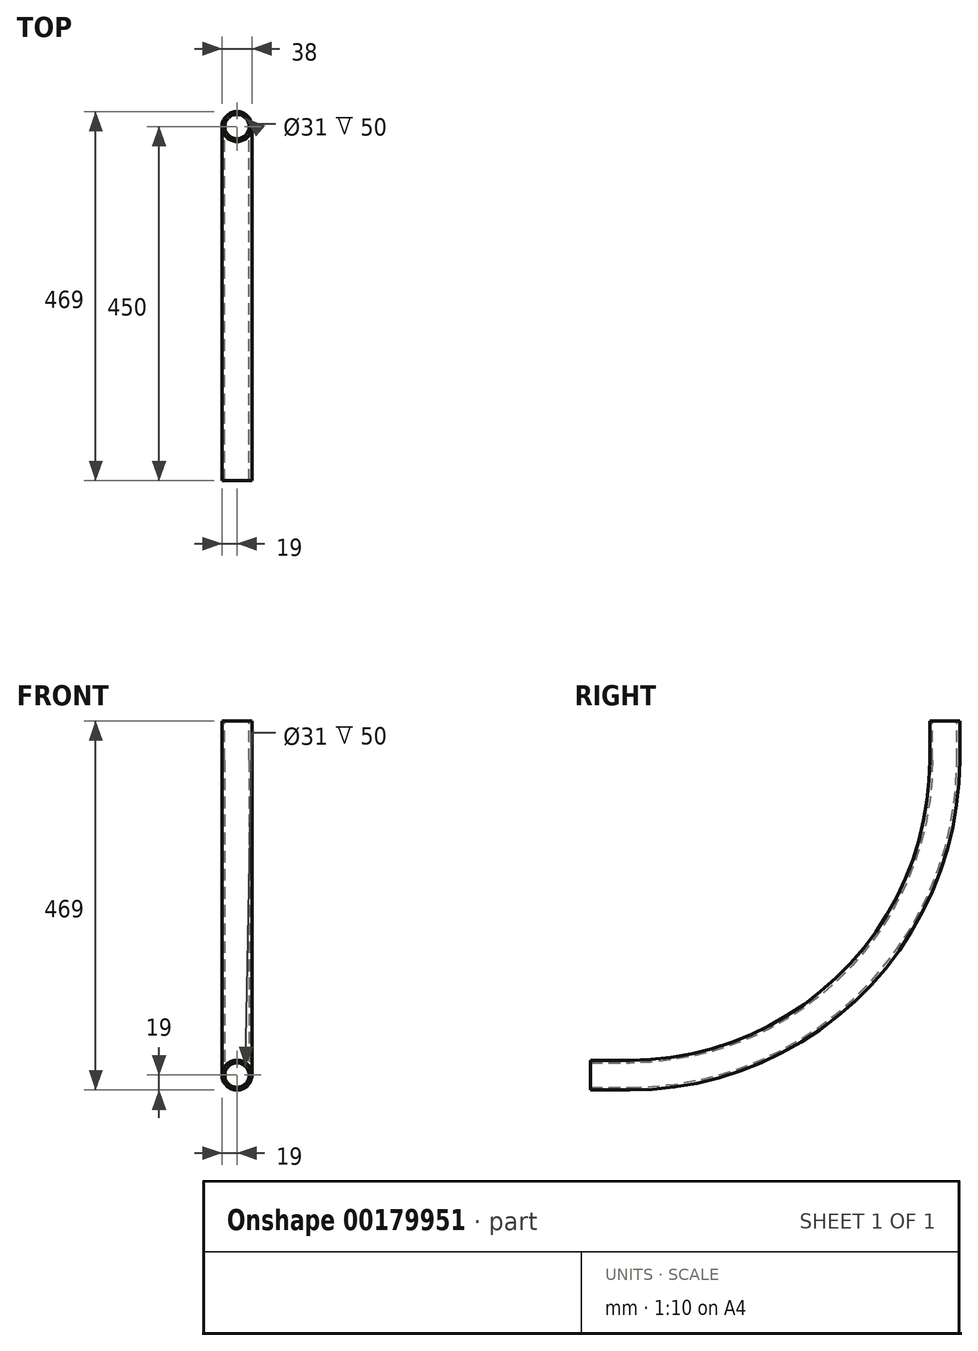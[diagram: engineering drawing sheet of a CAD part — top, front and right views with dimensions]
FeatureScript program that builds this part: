
annotation { "Feature Type Name" : "Feature", "Feature Type Description" : "" }
export const myFeature = defineFeature(function(context is Context, id is Id, definition is map)
    precondition{}
    {
        {
            var Q0;
            Q0=qCreatedBy(makeId("Front.planeOp"),FACE);
            var sketch = newSketch(context, id + "F0", { "sketchPlane" : qUnion([Q0])});
            skCircle(sketch, "E0", {"center": v(0, 0) * mm, "radius": 19 * mm});
            skCircle(sketch, "E1.0", {"center": v(0, 0) * mm, "radius": 15.5 * mm});
            skSolve(sketch);
        }
        {
            var Q0;
            Q0=qCreatedBy(makeId("Right.planeOp"),FACE);
            var sketch = newSketch(context, id + "F1", { "sketchPlane" : qUnion([Q0])});
            skLineSegment(sketch, "E2", {"start": v(0, 0) * mm, "end": v(50, 0) * mm});
            skArc(sketch, "E3", {"start": v(50, 0) * mm, "mid": v(332.84, 117.16) * mm, "end": v(450, 400) * mm});
            skLineSegment(sketch, "E4", {"start": v(450, 400) * mm, "end": v(450, 450) * mm});
            skSolve(sketch);
        }
        {
            var Q0;
            Q0=makeQuery(id+"F0.imprint","IMPRINT",FACE,{"disambiguationData":[TD([[makeQuery(id+"F0.imprint","IMPRINT",EDGE,{"derivedFrom":sQuery(id+"F0.wireOp",EDGE,"E0")}),1.0]])]});
            var Q1;
            Q1=sQuery(id+"F1.wireOp",EDGE,"E3");
            var Q2;
            Q2=sQuery(id+"F1.wireOp",EDGE,"E2");
            var Q3;
            Q3=sQuery(id+"F1.wireOp",EDGE,"E4");
            sweep(context, id + "F2", {"profiles" : qUnion([Q0]), "path" : qUnion([Q1, Q2, Q3])});
        }
    });
